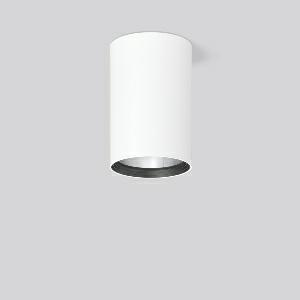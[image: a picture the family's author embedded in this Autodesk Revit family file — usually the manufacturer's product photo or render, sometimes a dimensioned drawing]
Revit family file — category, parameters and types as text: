
# Revit family: heledon_maxi_a_931237_002_48a7
name_source: partatom
category: Lighting Fixtures
units: mm (PartAtom-declared; Revit-internal decimal feet)

## family parameters
Cut with Voids When Loaded = No
Host = Face
Light Source = No
Part Type = Normal
Room Calculation Point = No
Round Connector Dimension = Use Diameter
Shared = No

## types (1)
- HELEDON maxi A (1 x LED Modul 920 meat+, 2200 lm, 2000)
    Apparent Load = 33 VA
    Approval mark = CE
    CIE Flux Codes = 100 100 100 100 100
    Color Rendering = 90
    Color Temperature = 2000
    Default Elevation = 1800 mm
    Description = Series: HELEDON maxi
Cylindrical surface-mounted downlight. Housing: die-cast aluminium, powder-coated. Internal ceiling frame polycarbonate with bayonet mounting. Black plastic ring and recessed LED to prevent glare from the side. Optical assembly with reflector made of MIRO-Silver with 98% total light reflection for outstanding efficiency - can be changed without tools. Special LED for illumination of meat included. Suitable for Ceiling mounting. Easy installation with a separate ceiling frame with bayonet mounting and plug connection. Driver integrated. Connected via plug-in connector. High quality converter without flickering and stroboscopic effect. The following accessories can be mounted without use of tools: interchangeable lenses, decorative glasses, honeycomb louvre, clear and frosted diffusers, white interchangeable plastic ring. 
Colour: traffic white, matt (RAL 9016)
Diameter: 123 mm
Height: 183 mm
Lamp: LED
Socket: without socket
Colour temperature: meat +
System power: 33 W
Rated luminous flux: 2200 lm
Luminous efficiency: 67 lm/W
Control gear: Regulated power supply
Protection class: I
Type of protection: IP 20
    Height = 183 mm
    Lamp = 1 x LED Modul 920 meat+
    Lamp Light Flux = 2200 lm
    Lamp count = 1
    Length = 123 mm
    Lifetime = 50000 h
    Luminous efficacy = 67 lm/W
    Manufacturer = RZB
    ModVariant = No
    Model = 931237.002
    Mounting Place = Ceiling
    Mounting Type = Surface mounted
    Number of Poles = 1
    OnlyDefault = Yes
    Power Factor = 1
    Product Name = HELEDON maxi A
    Product group = Surface mounted downlights
    ProductGroupID = 302
    Protection Class = Protection class I
    Protection Degree = IP 20
    RLX_Detail_Level = 1
    RLX_Emergency_Light_Flux = 0 lm
    RLX_Emergency_Type = 0
    RLX_Emergency_Type_DB = No
    RlxData = <blob elided: 96829 chars, md5=eda3fc6c>
    Socket = socket
    Standby Power = 0 W
    System Light Flux = 2200 lm
    System Power = 33 W
    Type Comments = Product without accessories
    Type Image = 931192.002.jpg
    URL = http://relux.com
    VarID = ---
    Voltage = 230 V
    Voltage Range = 220-240 V
    Weight = 0.00 kg
    Width = 0 mm  [stored 0 ft]

note: [stored X ft] marks values corroborated as IEEE doubles in the binary element streams (Revit-internal decimal feet)

## geometry (parser evidence)
native form markers: Blend x4, Sweep x10
no freeform markers — native parametric forms only
